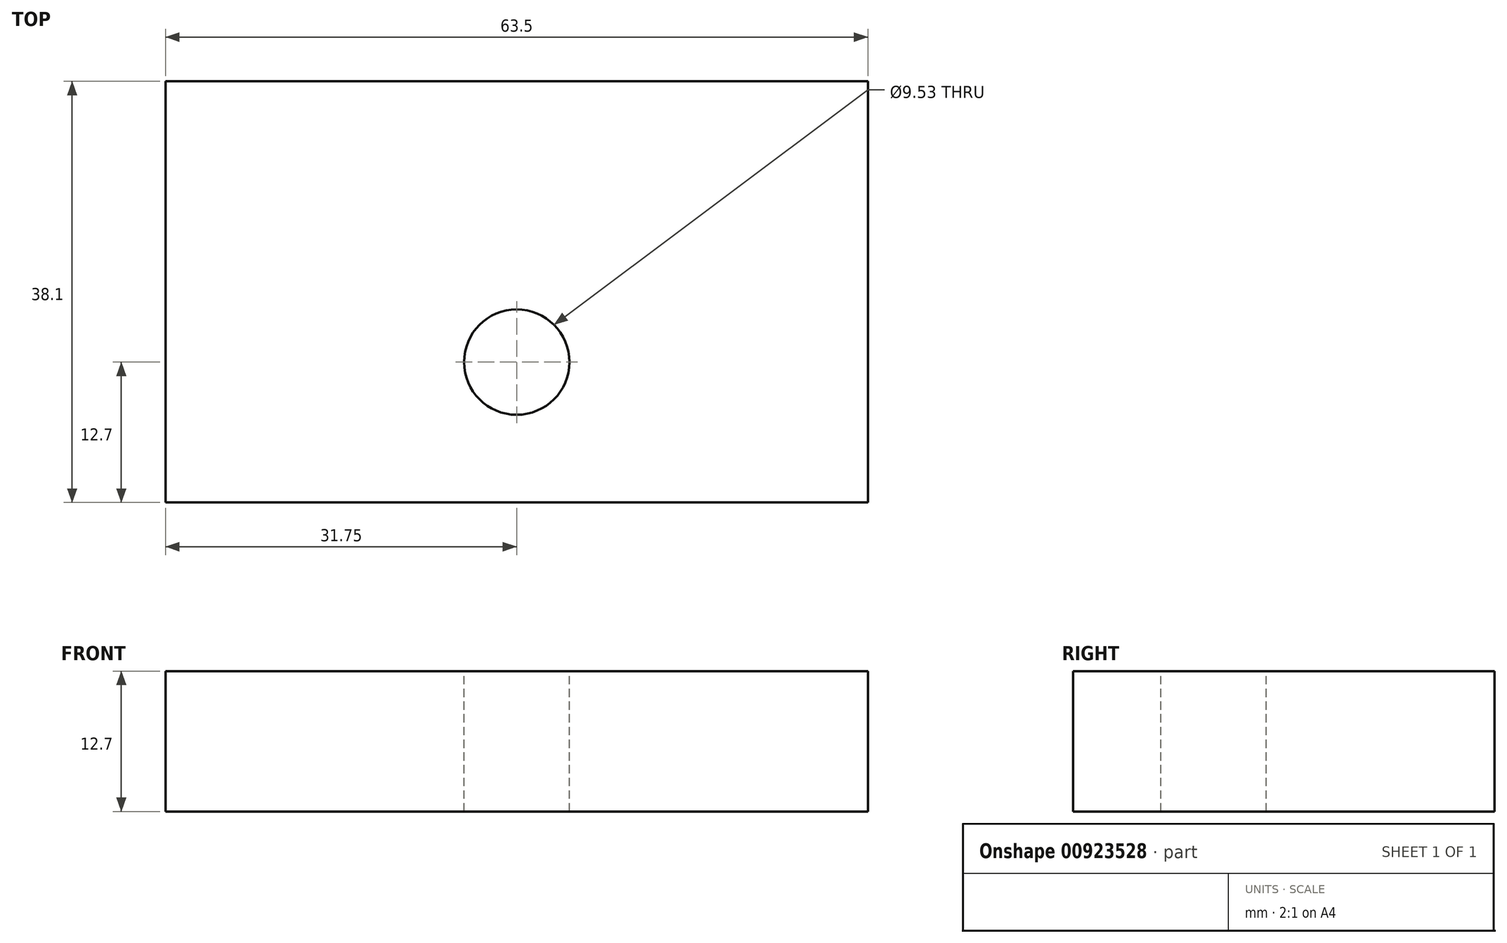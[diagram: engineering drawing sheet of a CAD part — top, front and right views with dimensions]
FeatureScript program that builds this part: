
annotation { "Feature Type Name" : "Feature", "Feature Type Description" : "" }
export const myFeature = defineFeature(function(context is Context, id is Id, definition is map)
    precondition{}
    {
        {
            var Q0;
            Q0=qCreatedBy(makeId("Top.planeOp"),FACE);
            var sketch = newSketch(context, id + "F0", { "sketchPlane" : qUnion([Q0])});
            skLineSegment(sketch, "E0.bottom", {"start": v(31.75, 19.05) * mm, "end": v(-31.75, 19.05) * mm});
            skLineSegment(sketch, "E0.top", {"start": v(31.75, -19.05) * mm, "end": v(-31.75, -19.05) * mm});
            skLineSegment(sketch, "E0.left", {"start": v(31.75, 19.05) * mm, "end": v(31.75, -19.05) * mm});
            skLineSegment(sketch, "E0.right", {"start": v(-31.75, 19.05) * mm, "end": v(-31.75, -19.05) * mm});
            skPoint(sketch, "E0.middle", {"position": v(0, 0) * mm});
            skLineSegment(sketch, "E1.bottom", {"start": v(1.92, -19.05) * mm, "end": v(1.51, -19.05) * mm});
            skSolve(sketch);
        }
        {
            var Q0;
            Q0=makeQuery(id+"F0.imprint","IMPRINT",FACE,{"disambiguationData":[TD([[makeQuery(id+"F0.imprint","IMPRINT",EDGE,{"derivedFrom":sQuery(id+"F0.wireOp",EDGE,"E0.bottom")}),1.0]])]});
            extrude(context, id + "F1", {"entities" : qUnion([Q0]), "depth" : 12.7 * mm, "offsetDistance" : 25.4 * mm});
        }
        {
            var Q0;
            Q0=makeQuery(id+"F1.opExtrude","CAP_FACE",FACE,{"disambiguationData":[OSD([sQuery(id+"F0.wireOp",EDGE,"E0.bottom"),sQuery(id+"F0.wireOp",EDGE,"E0.top"),sQuery(id+"F0.wireOp",EDGE,"E0.left"),sQuery(id+"F0.wireOp",EDGE,"E0.right"),sQuery(id+"F0.wireOp",EDGE,"E1.bottom")])],"isStart":false});
            var sketch = newSketch(context, id + "F2", { "sketchPlane" : qUnion([Q0])});
            skCircle(sketch, "E2", {"center": v(0, -6.35) * mm, "radius": 4.76 * mm});
            skSolve(sketch);
        }
        {
            var Q0;
            Q0=makeQuery(id+"F2.imprint","IMPRINT",FACE,{"disambiguationData":[TD([[makeQuery(id+"F2.imprint","IMPRINT",EDGE,{"derivedFrom":sQuery(id+"F2.wireOp",EDGE,"E2")}),1.0]])]});
            extrude(context, id + "F3", {"entities" : qUnion([Q0]), "operationType" : NewBodyOperationType.REMOVE, "oppositeDirection" : true, "depth" : 25.4 * mm, "offsetDistance" : 25.4 * mm});
        }
    });
